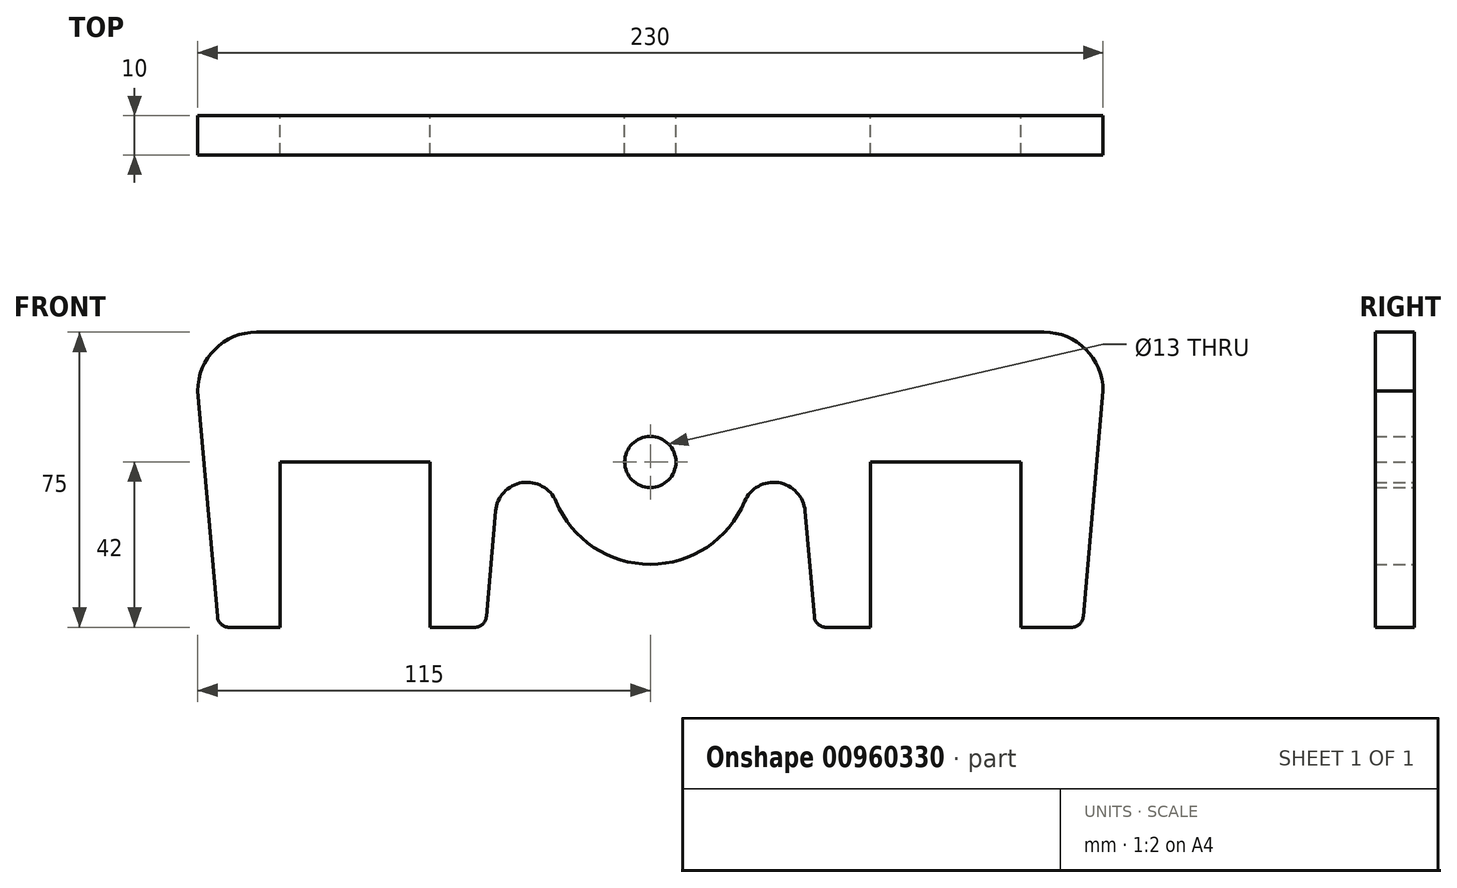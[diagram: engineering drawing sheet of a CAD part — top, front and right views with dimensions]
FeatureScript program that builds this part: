
annotation { "Feature Type Name" : "Feature", "Feature Type Description" : "" }
export const myFeature = defineFeature(function(context is Context, id is Id, definition is map)
    precondition{}
    {
        {
            var Q0;
            Q0=qCreatedBy(makeId("Front.planeOp"),FACE);
            var sketch = newSketch(context, id + "F0", { "sketchPlane" : qUnion([Q0])});
            skLineSegment(sketch, "E0.bottom", {"start": v(-44.65, -37.5) * mm, "end": v(-55.9, -37.5) * mm});
            skLineSegment(sketch, "E0.top", {"start": v(0, 37.5) * mm, "end": v(-100, 37.5) * mm, "construction": true});
            skPoint(sketch, "E0.middle", {"position": v(0, 0) * mm});
            skLineSegment(sketch, "E1.top", {"start": v(-94.1, 4.5) * mm, "end": v(-55.9, 4.5) * mm});
            skLineSegment(sketch, "E1.left", {"start": v(-94.1, -37.5) * mm, "end": v(-94.1, 4.5) * mm});
            skLineSegment(sketch, "E1.right", {"start": v(-55.9, -37.5) * mm, "end": v(-55.9, 4.5) * mm});
            skPoint(sketch, "E2.visualSharp", {"position": v(-115, 37.5) * mm});
            skArc(sketch, "E2.filletArc", {"start": v(-100, 37.5) * mm, "mid": v(-110.6, 33.1) * mm, "end": v(-115, 22.5) * mm});
            skLineSegment(sketch, "E3", {"start": v(-115, 22.5) * mm, "end": v(-110, -34.76) * mm});
            skPoint(sketch, "E4.newPointA", {"position": v(-115, -37.5) * mm});
            skArc(sketch, "E4.filletArc", {"start": v(-110, -34.76) * mm, "mid": v(-109.03, -36.71) * mm, "end": v(-107, -37.5) * mm});
            skLineSegment(sketch, "E5", {"start": v(-41.66, -34.76) * mm, "end": v(-39.32, -7.97) * mm});
            skArc(sketch, "E6", {"start": v(-23.97, -5.57) * mm, "mid": v(-14.4, -17.15) * mm, "end": v(0, -21.5) * mm});
            skPoint(sketch, "E7.newPointA", {"position": v(115, -37.5) * mm});
            skPoint(sketch, "E7.newPointB", {"position": v(-41.9, -37.5) * mm});
            skArc(sketch, "E7.filletArc", {"start": v(-44.65, -37.5) * mm, "mid": v(-42.62, -36.71) * mm, "end": v(-41.66, -34.76) * mm});
            skPoint(sketch, "E0.left.end.orphan", {"position": v(115, 37.5) * mm});
            skLineSegment(sketch, "E8", {"start": v(-100, 37.5) * mm, "end": v(0, 37.5) * mm});
            skArc(sketch, "E9", {"start": v(-23.97, -5.57) * mm, "mid": v(-32.58, -0.76) * mm, "end": v(-39.32, -7.97) * mm});
            skArc(sketch, "E10", {"start": v(0, 11) * mm, "mid": v(-6.5, 4.5) * mm, "end": v(0, -2) * mm});
            skLineSegment(sketch, "E11.trimOffspring", {"start": v(-94.1, -37.5) * mm, "end": v(-107, -37.5) * mm});
            skArc(sketch, "E12.MirrorCS", {"start": v(110, -34.76) * mm, "mid": v(109.03, -36.71) * mm, "end": v(107, -37.5) * mm});
            skArc(sketch, "E13.MirrorCS", {"start": v(44.65, -37.5) * mm, "mid": v(42.62, -36.71) * mm, "end": v(41.66, -34.76) * mm});
            skLineSegment(sketch, "E14.MirrorCS", {"start": v(0, 37.5) * mm, "end": v(100, 37.5) * mm, "construction": true});
            skPoint(sketch, "E15.MirrorP", {"position": v(41.9, -37.5) * mm});
            skArc(sketch, "E16.MirrorCS", {"start": v(0, 11) * mm, "mid": v(6.5, 4.5) * mm, "end": v(0, -2) * mm});
            skLineSegment(sketch, "E17.MirrorCS", {"start": v(94.1, -37.5) * mm, "end": v(94.1, 4.5) * mm});
            skArc(sketch, "E18.MirrorCS", {"start": v(100, 37.5) * mm, "mid": v(110.6, 33.1) * mm, "end": v(115, 22.5) * mm});
            skLineSegment(sketch, "E19.MirrorCS", {"start": v(44.65, -37.5) * mm, "end": v(55.9, -37.5) * mm});
            skArc(sketch, "E20.MirrorCS", {"start": v(23.97, -5.57) * mm, "mid": v(32.58, -0.76) * mm, "end": v(39.32, -7.97) * mm});
            skLineSegment(sketch, "E21.MirrorCS", {"start": v(94.1, 4.5) * mm, "end": v(55.9, 4.5) * mm});
            skLineSegment(sketch, "E22.MirrorCS", {"start": v(94.1, -37.5) * mm, "end": v(107, -37.5) * mm});
            skLineSegment(sketch, "E23.MirrorCS", {"start": v(55.9, -37.5) * mm, "end": v(55.9, 4.5) * mm});
            skLineSegment(sketch, "E24.MirrorCS", {"start": v(115, 22.5) * mm, "end": v(110, -34.76) * mm});
            skLineSegment(sketch, "E25.MirrorCS", {"start": v(100, 37.5) * mm, "end": v(0, 37.5) * mm});
            skLineSegment(sketch, "E26.MirrorCS", {"start": v(41.66, -34.76) * mm, "end": v(39.32, -7.97) * mm});
            skArc(sketch, "E27.MirrorCS", {"start": v(23.97, -5.57) * mm, "mid": v(14.4, -17.15) * mm, "end": v(0, -21.5) * mm});
            skSolve(sketch);
        }
        {
            var Q0;
            Q0=makeQuery(id+"F0.imprint","IMPRINT",FACE,{"disambiguationData":[TD([[makeQuery(id+"F0.imprint","IMPRINT",EDGE,{"derivedFrom":sQuery(id+"F0.wireOp",EDGE,"E0.bottom")}),-1.0]])]});
            extrude(context, id + "F1", {"entities" : qUnion([Q0]), "depth" : 10 * mm, "offsetDistance" : 25 * mm});
        }
    });
